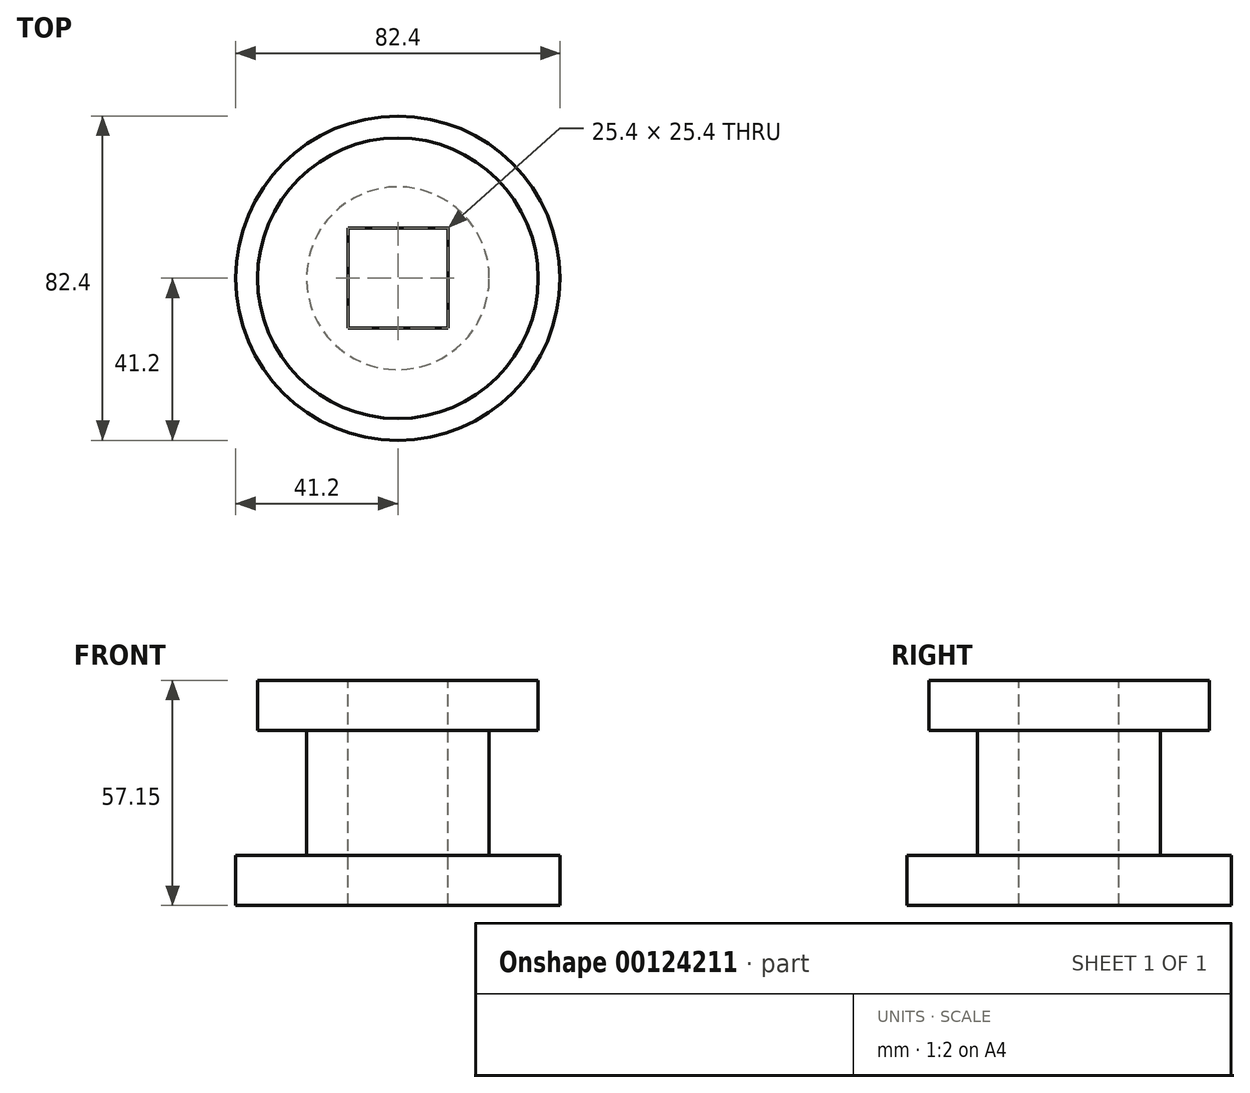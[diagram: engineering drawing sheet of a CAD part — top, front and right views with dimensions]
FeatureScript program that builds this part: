
annotation { "Feature Type Name" : "Feature", "Feature Type Description" : "" }
export const myFeature = defineFeature(function(context is Context, id is Id, definition is map)
    precondition{}
    {
        {
            var Q0;
            Q0=qCreatedBy(makeId("Top.planeOp"),FACE);
            var sketch = newSketch(context, id + "F0", { "sketchPlane" : qUnion([Q0])});
            skCircle(sketch, "E0", {"center": v(0, 0) * mm, "radius": 41.2 * mm});
            skSolve(sketch);
        }
        {
            var Q0;
            Q0 = qSketchRegion(id + "F0", true);
            extrude(context, id + "F1", {"entities" : qUnion([Q0]), "depth" : 12.7 * mm});
        }
        {
            var Q0;
            Q0=qCreatedBy(makeId("Top.planeOp"),FACE);
            var sketch = newSketch(context, id + "F2", { "sketchPlane" : qUnion([Q0])});
            skCircle(sketch, "E1", {"center": v(0, 0) * mm, "radius": 23.23 * mm});
            skSolve(sketch);
        }
        {
            var Q0;
            Q0 = qSketchRegion(id + "F2", true);
            extrude(context, id + "F3", {"entities" : qUnion([Q0]), "operationType" : NewBodyOperationType.ADD, "depth" : 44.45 * mm});
        }
        {
            var Q0;
            Q0=makeQuery(id+"F3.opExtrude","CAP_FACE",FACE,{"disambiguationData":[OSD([sQuery(id+"F2.wireOp",EDGE,"E1")])],"isStart":false});
            var sketch = newSketch(context, id + "F4", { "sketchPlane" : qUnion([Q0])});
            skCircle(sketch, "E2", {"center": v(0, 0) * mm, "radius": 35.65 * mm});
            skSolve(sketch);
        }
        {
            var Q0;
            Q0 = qSketchRegion(id + "F4", true);
            extrude(context, id + "F5", {"entities" : qUnion([Q0]), "operationType" : NewBodyOperationType.ADD, "depth" : 12.7 * mm});
        }
        {
            var Q0;
            Q0=makeQuery(id+"F5.opExtrude","CAP_FACE",FACE,{"disambiguationData":[OSD([sQuery(id+"F4.wireOp",EDGE,"E2")])],"isStart":false});
            var sketch = newSketch(context, id + "F6", { "sketchPlane" : qUnion([Q0])});
            skLineSegment(sketch, "E3.bottom", {"start": v(-12.7, -12.7) * mm, "end": v(12.7, -12.7) * mm});
            skLineSegment(sketch, "E3.top", {"start": v(-12.7, 12.7) * mm, "end": v(12.7, 12.7) * mm});
            skLineSegment(sketch, "E3.left", {"start": v(-12.7, -12.7) * mm, "end": v(-12.7, 12.7) * mm});
            skLineSegment(sketch, "E3.right", {"start": v(12.7, -12.7) * mm, "end": v(12.7, 12.7) * mm});
            skPoint(sketch, "E3.middle", {"position": v(0, 0) * mm});
            skSolve(sketch);
        }
        {
            var Q0;
            Q0 = qSketchRegion(id + "F6", true);
            extrude(context, id + "F7", {"entities" : qUnion([Q0]), "operationType" : NewBodyOperationType.REMOVE, "endBound" : BoundingType.THROUGH_ALL, "oppositeDirection" : true, "depth" : 25.4 * mm});
        }
    });
